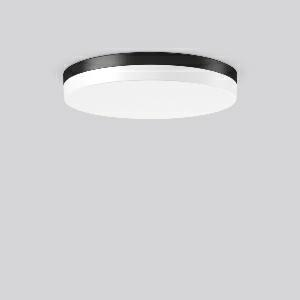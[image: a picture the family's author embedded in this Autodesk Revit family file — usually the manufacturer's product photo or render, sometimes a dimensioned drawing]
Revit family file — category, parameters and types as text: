
# Revit family: flat_slim_round_312633_0031_3223
name_source: partatom
category: Lighting Fixtures
units: mm (PartAtom-declared; Revit-internal decimal feet)

## family parameters
Cut with Voids When Loaded = No
Host = Face
Light Source = No
Part Type = Normal
Room Calculation Point = No
Round Connector Dimension = Use Diameter
Shared = No

## types (1)
- MultiLumen 1 830 (1 x LED Modul 830, 3350 lm, 3000)
    Apparent Load = 31 VA
    CIE Flux Codes = 41 71 90 86 100
    Color Rendering = 80
    Color Temperature = 3000
    Default Elevation = 1800 mm
    Height = 75 mm
    Lamp = 1 x LED Modul 830
    Lamp Light Flux = 3350 lm
    Lamp count = 1
    Length = 480 mm
    Lifetime = 50000 h
    Luminous efficacy = 108 lm/W
    Manufacturer = RZB
    ModVariant = No
    Model = 312633.0031
    Mounting Place = Ceiling
    Mounting Type = Surface mounted
    Number of Poles = 1
    OnlyDefault = Yes
    Power Factor = 1
    Product Name = FLAT SLIM round
    Product group = Surface mounted ceiling and wall luminaires
    ProductGroupID = 305
    Protection Class = Protection class I
    Protection Degree = Degree of protection
    RLX_Detail_Level = 1
    RLX_Emergency_Light_Flux = 0 lm
    RLX_Emergency_Type = 0
    RLX_Emergency_Type_DB = No
    RlxData = <blob elided: 23013 chars, md5=a8b37c8d>
    Socket = socket
    Standby Power = 0 W
    System Light Flux = 3350 lm
    System Power = 31 W
    Type Comments = MultiLumen 1 830
    Type Image = 312633.0031.jpg
    URL = http://relux.com
    VarID = multilumen_1_830
    Voltage = 0 V
    Weight = 0.00 kg
    Width = 0 mm  [stored 0 ft]

note: [stored X ft] marks values corroborated as IEEE doubles in the binary element streams (Revit-internal decimal feet)

## geometry (parser evidence)
native form markers: Blend x4, Sweep x13
no freeform markers — native parametric forms only
